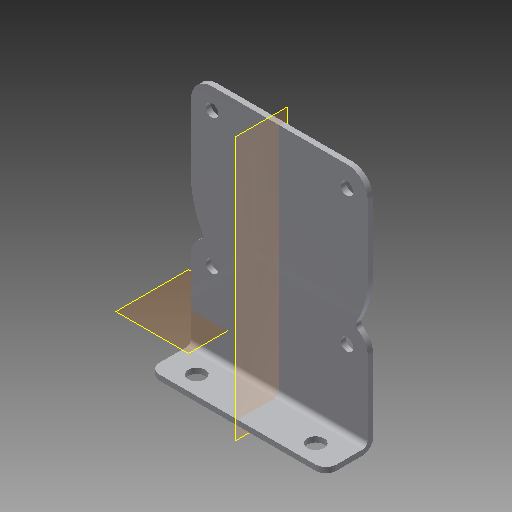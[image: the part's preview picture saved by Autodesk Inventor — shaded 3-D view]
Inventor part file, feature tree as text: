
AUTODESK INVENTOR PART (.ipt)
format: ipt  version: 2017 (Build 210142000, 142)  size: 186,368 bytes
history: native  units: in
note: dims shown in document units (in); Inventor stores cm internally (conversion verified against a paired STEP export)
features: sketch x6, extrude x4, fillet x3, hole x2, reference x2, plane x1, mirror x1
ambient origin geometry x8: Origin, YZ Plane, XZ Plane, XY Plane, X Axis, Y Axis, Z Axis, Center Point
bodies: Solid1 (feature_tree)
feature tree (19):
  extrude  "Extrusion1"  Depth=2.11in
  extrude  "Extrusion5"  Depth=2.11in
  extrude  "Extrusion2"  Depth=0.5in TaperAngle=0.0deg
  extrude  "Extrusion4"  Depth=0.25in TaperAngle=0.0deg
  hole  "Hole3"  [1 undecoded]
  plane  "Work Plane1"
  fillet  "Fillet3"  Radius=0.063in
  fillet  "Fillet4"  Radius=0.125in
  fillet  "Fillet5"  Radius=0.125in
  hole  "Hole6"  [1 undecoded]
  mirror  "Mirror1"
  sketch  "Sketch1"  dims[d0=2.11in d1=2.5in]
  sketch  "Sketch2"  dims[d2=0.0625in d3=0.0in d4=2.11in]
  sketch  "Sketch6"  dims[d6=0.5in d7=0.0in d29=1.0in d30=0.0in]
  reference  "Reference2"
  sketch  "Sketch7"  dims[d31=0.15in d32=0.75in d33=0.279in d34=0.25in d35=0.5635in d36=1.0in d37=0.8108in d57=1.0in d58=0.0in]
  sketch  "Sketch9"  dims[d59=0.063in d60=2.856in d61=0.063in d62=0.125in d63=0.125in]
  sketch  "Sketch10"  dims[d64=0.201in d65=0.75in d66=0.385in d67=0.25in d68=0.5635in d69=1.0in d70=0.8108in]
  reference  "Reference3"
note: 2 required parameter values undecoded (feature->parameter linkage not recoverable at this tier; creation-order binding heuristic only, values carry confidence <= 0.55)
